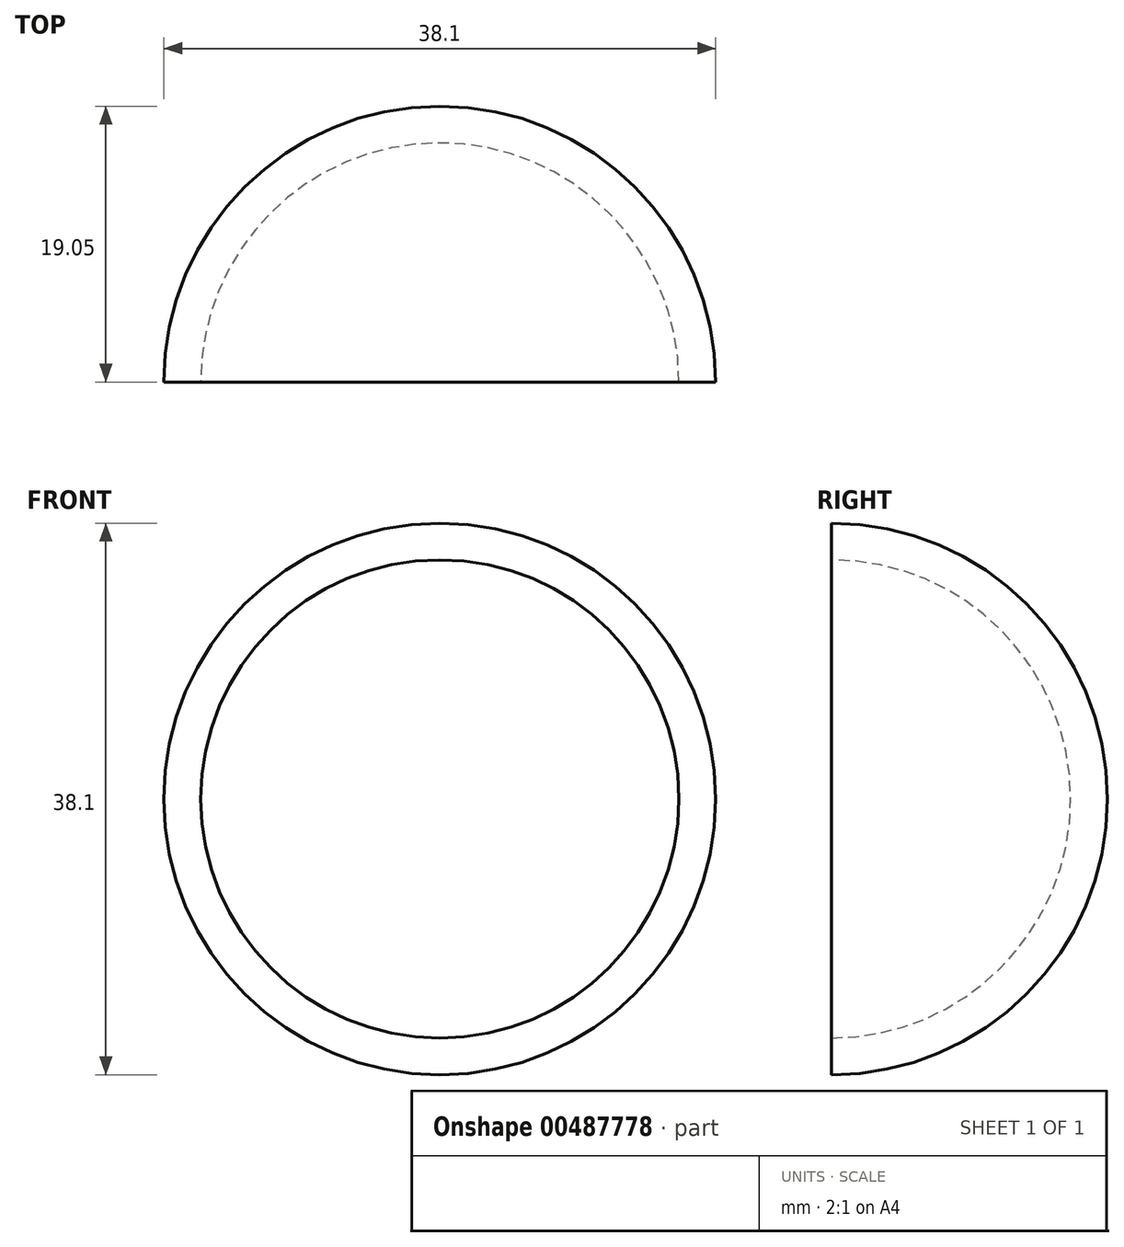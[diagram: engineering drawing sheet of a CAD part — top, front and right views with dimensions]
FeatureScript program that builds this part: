
annotation { "Feature Type Name" : "Feature", "Feature Type Description" : "" }
export const myFeature = defineFeature(function(context is Context, id is Id, definition is map)
    precondition{}
    {
        {
            var Q0;
            Q0=qCreatedBy(makeId("Front.planeOp"),FACE);
            var sketch = newSketch(context, id + "F0", { "sketchPlane" : qUnion([Q0])});
            skArc(sketch, "E0", {"start": v(0, -19.05) * mm, "mid": v(19.05, 0) * mm, "end": v(0, 19.05) * mm});
            skLineSegment(sketch, "E1", {"start": v(0, 19.05) * mm, "end": v(0, -19.05) * mm});
            skLineSegment(sketch, "E2", {"start": v(0, 0) * mm, "end": v(0, 48.06) * mm, "construction": true});
            skSolve(sketch);
        }
        {
            var Q0;
            Q0 = qSketchRegion(id + "F0", true);
            var Q1;
            Q1=sQuery(id+"F0.wireOp",EDGE,"E2");
            revolve(context, id + "F1", {"entities" : qUnion([Q0]), "axis" : qUnion([Q1]), "revolveType" : RevolveType.ONE_DIRECTION, "angle" : 180 * degree});
        }
        {
            var Q0;
            Q0=makeQuery(id+"F1.opRevolve","CAP_FACE",FACE,{"disambiguationData":[OSD([sQuery(id+"F0.wireOp",EDGE,"E0"),sQuery(id+"F0.wireOp",EDGE,"E1")])],"isStart":true});
            shell(context, id + "F2", {"entities" : qUnion([Q0]), "thickness" : 2.54 * mm});
        }
    });
